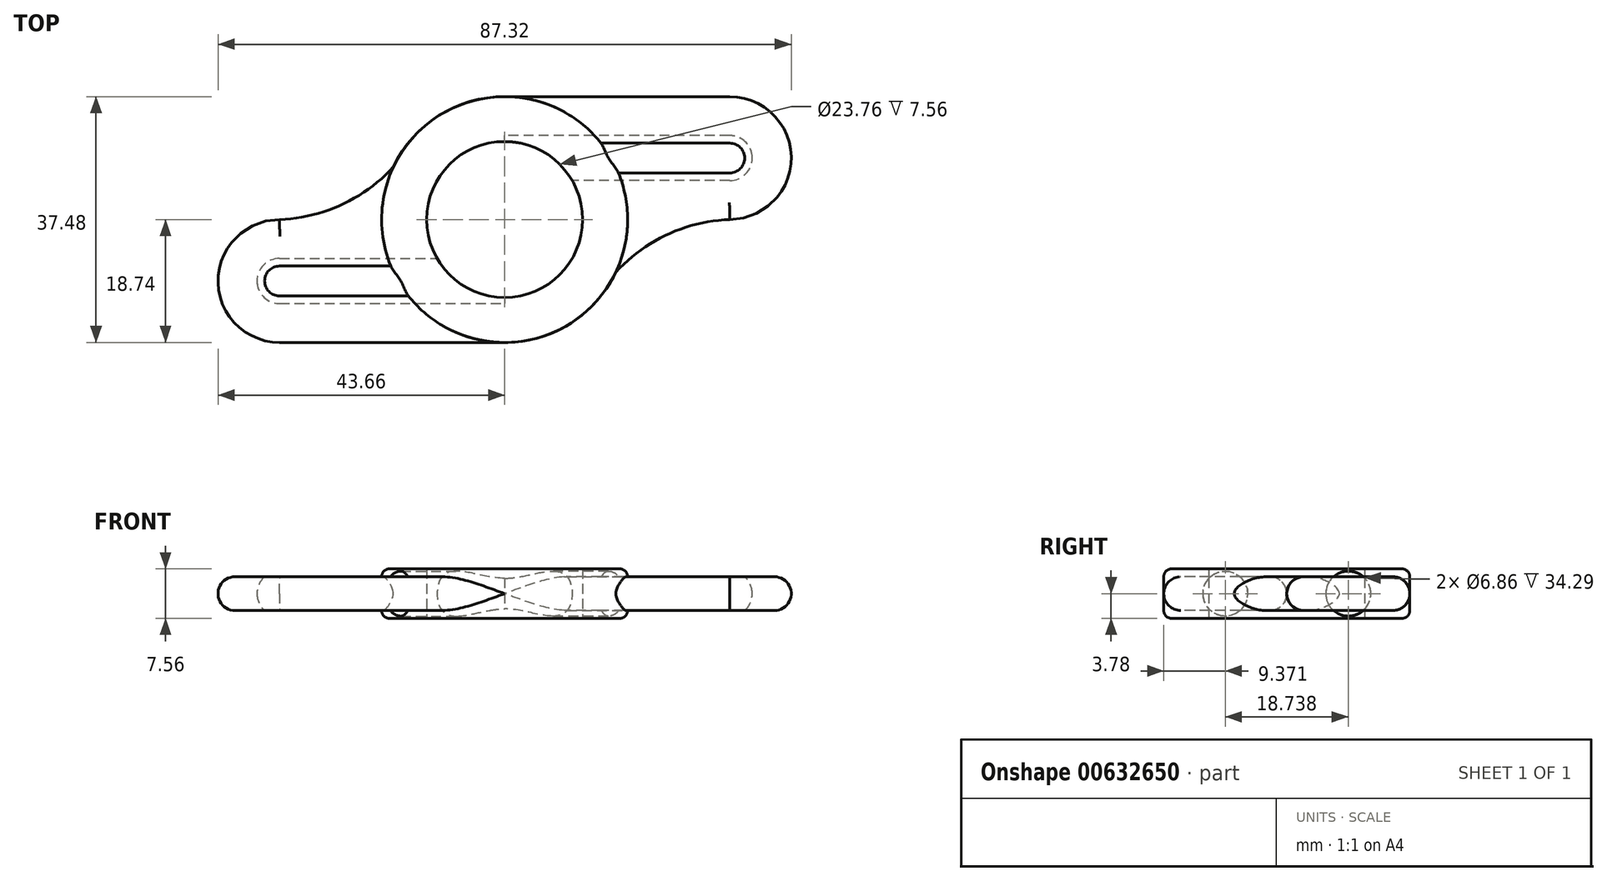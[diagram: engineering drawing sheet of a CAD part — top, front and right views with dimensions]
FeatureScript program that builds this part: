
annotation { "Feature Type Name" : "Feature", "Feature Type Description" : "" }
export const myFeature = defineFeature(function(context is Context, id is Id, definition is map)
    precondition{}
    {
        {
            var Q0;
            Q0=qCreatedBy(makeId("Top.planeOp"),FACE);
            var sketch = newSketch(context, id + "F0", { "sketchPlane" : qUnion([Q0])});
            skCircle(sketch, "E0", {"center": v(0, 0) * mm, "radius": 11.88 * mm});
            skCircle(sketch, "E1", {"center": v(0, 0) * mm, "radius": 18.74 * mm});
            skLineSegment(sketch, "E2", {"start": v(0, 0) * mm, "end": v(0, -18.74) * mm});
            skLineSegment(sketch, "E3", {"start": v(0, -18.74) * mm, "end": v(-34.3, -18.74) * mm});
            skLineSegment(sketch, "E4", {"start": v(-34.3, -18.74) * mm, "end": v(-34.3, 0) * mm});
            skLineSegment(sketch, "E5", {"start": v(-34.3, 0) * mm, "end": v(0, 0) * mm});
            skPoint(sketch, "E6", {"position": v(-34.3, -9.37) * mm});
            skCircle(sketch, "E7", {"center": v(-34.3, -9.37) * mm, "radius": 9.37 * mm});
            skLineSegment(sketch, "E8", {"start": v(0, 0) * mm, "end": v(0, 18.74) * mm});
            skLineSegment(sketch, "E9", {"start": v(0, 18.74) * mm, "end": v(34.3, 18.74) * mm});
            skLineSegment(sketch, "E10", {"start": v(34.3, 18.74) * mm, "end": v(34.3, 0) * mm});
            skLineSegment(sketch, "E11", {"start": v(34.3, 0) * mm, "end": v(0, 0) * mm});
            skPoint(sketch, "E12", {"position": v(34.3, 9.37) * mm});
            skCircle(sketch, "E13", {"center": v(34.3, 9.37) * mm, "radius": 9.37 * mm});
            skLineSegment(sketch, "E14", {"start": v(-18.74, 0) * mm, "end": v(-18.74, 17.97) * mm});
            skLineSegment(sketch, "E15", {"start": v(18.74, 0) * mm, "end": v(18.74, -17.25) * mm});
            skPoint(sketch, "E16", {"position": v(-18.74, 6.25) * mm});
            skPoint(sketch, "E17", {"position": v(18.74, -6.25) * mm});
            skLineSegment(sketch, "E18", {"start": v(0, 0) * mm, "end": v(-13.25, 13.25) * mm});
            skLineSegment(sketch, "E19", {"start": v(0, 0) * mm, "end": v(13.25, -13.25) * mm});
            skArc(sketch, "E20", {"start": v(-34.3, 0) * mm, "mid": v(-24.81, 2.27) * mm, "end": v(-16.94, 8.02) * mm});
            skArc(sketch, "E21", {"start": v(34.3, 0) * mm, "mid": v(24.81, -2.27) * mm, "end": v(16.94, -8.02) * mm});
            skSolve(sketch);
        }
        {
            var Q0;
            {var subQ3=sQuery(id+"F0.wireOp",EDGE,"E0");var subQ5=sQuery(id+"F0.wireOp",EDGE,"E18");var subQ8=makeQuery(id+"F0.imprint","INTERSECT",VERTEX,{"derivedFrom":[subQ3,subQ5]});Q0=makeQuery(id+"F0.imprint","IMPRINT",FACE,{"disambiguationData":[TD([[makeQuery(id+"F0.imprint","IMPRINT",EDGE,{"disambiguationData":[TD([[subQ8,-1.0]])],"derivedFrom":subQ3}),-1.0]])]});}
            var Q1;
            {var subQ0=sQuery(id+"F0.wireOp",EDGE,"E8");var subQ1=sQuery(id+"F0.wireOp",EDGE,"E0");var subQ2=makeQuery(id+"F0.imprint","INTERSECT",VERTEX,{"derivedFrom":[subQ1,subQ0]});Q1=makeQuery(id+"F0.imprint","IMPRINT",FACE,{"disambiguationData":[TD([[makeQuery(id+"F0.imprint","IMPRINT",EDGE,{"disambiguationData":[TD([[subQ2,-1.0]])],"derivedFrom":subQ1}),-1.0]])]});}
            var Q2;
            {var subQ0=sQuery(id+"F0.wireOp",EDGE,"E8");var subQ1=sQuery(id+"F0.wireOp",EDGE,"E0");var subQ2=makeQuery(id+"F0.imprint","INTERSECT",VERTEX,{"derivedFrom":[subQ1,subQ0]});Q2=makeQuery(id+"F0.imprint","IMPRINT",FACE,{"disambiguationData":[TD([[makeQuery(id+"F0.imprint","IMPRINT",EDGE,{"disambiguationData":[TD([[subQ2,1.0]])],"derivedFrom":subQ1}),-1.0]])]});}
            var Q3;
            {var subQ0=sQuery(id+"F0.wireOp",EDGE,"E11");var subQ3=sQuery(id+"F0.wireOp",EDGE,"E0");var subQ4=makeQuery(id+"F0.imprint","INTERSECT",VERTEX,{"derivedFrom":[subQ3,subQ0]});Q3=makeQuery(id+"F0.imprint","IMPRINT",FACE,{"disambiguationData":[TD([[makeQuery(id+"F0.imprint","IMPRINT",EDGE,{"disambiguationData":[TD([[subQ4,1.0]])],"derivedFrom":subQ3}),-1.0]])]});}
            var Q4;
            {var subQ0=sQuery(id+"F0.wireOp",EDGE,"E2");var subQ1=sQuery(id+"F0.wireOp",EDGE,"E0");var subQ2=makeQuery(id+"F0.imprint","INTERSECT",VERTEX,{"derivedFrom":[subQ1,subQ0]});Q4=makeQuery(id+"F0.imprint","IMPRINT",FACE,{"disambiguationData":[TD([[makeQuery(id+"F0.imprint","IMPRINT",EDGE,{"disambiguationData":[TD([[subQ2,-1.0]])],"derivedFrom":subQ1}),-1.0]])]});}
            var Q5;
            {var subQ0=sQuery(id+"F0.wireOp",EDGE,"E5");var subQ1=sQuery(id+"F0.wireOp",EDGE,"E0");var subQ2=makeQuery(id+"F0.imprint","INTERSECT",VERTEX,{"derivedFrom":[subQ1,subQ0]});Q5=makeQuery(id+"F0.imprint","IMPRINT",FACE,{"disambiguationData":[TD([[makeQuery(id+"F0.imprint","IMPRINT",EDGE,{"disambiguationData":[TD([[subQ2,-1.0]])],"derivedFrom":subQ1}),-1.0]])]});}
            extrude(context, id + "F1", {"entities" : qUnion([Q0, Q1, Q2, Q3, Q4, Q5]), "endBound" : BoundingType.SYMMETRIC, "depth" : 7 * mm * 1.08, "offsetDistance" : 25.4 * mm});
        }
        {
            var Q0;
            {var subQ0=sQuery(id+"F0.wireOp",EDGE,"E9");Q0=makeQuery(id+"F0.imprint","IMPRINT",FACE,{"disambiguationData":[TD([[makeQuery(id+"F0.imprint","IMPRINT",EDGE,{"derivedFrom":subQ0}),-1.0]])]});}
            var Q1;
            {var subQ0=sQuery(id+"F0.wireOp",EDGE,"E10");Q1=makeQuery(id+"F0.imprint","IMPRINT",FACE,{"disambiguationData":[TD([[makeQuery(id+"F0.imprint","IMPRINT",EDGE,{"derivedFrom":subQ0}),-1.0]])]});}
            var Q2;
            {var subQ0=sQuery(id+"F0.wireOp",EDGE,"E10");Q2=makeQuery(id+"F0.imprint","IMPRINT",FACE,{"disambiguationData":[TD([[makeQuery(id+"F0.imprint","IMPRINT",EDGE,{"derivedFrom":subQ0}),1.0]])]});}
            var Q3;
            {var subQ0=sQuery(id+"F0.wireOp",EDGE,"E21");var subQ3=sQuery(id+"F0.wireOp",EDGE,"E15");var subQ5=makeQuery(id+"F0.imprint","INTERSECT",VERTEX,{"derivedFrom":[subQ3,subQ0]});Q3=makeQuery(id+"F0.imprint","IMPRINT",FACE,{"disambiguationData":[TD([[makeQuery(id+"F0.imprint","IMPRINT",EDGE,{"disambiguationData":[TD([[subQ5,1.0]])],"derivedFrom":subQ3}),1.0]])]});}
            var Q4;
            {var subQ1=sQuery(id+"F0.wireOp",EDGE,"E1");var subQ3=sQuery(id+"F0.wireOp",EDGE,"E21");var subQ4=makeQuery(id+"F0.imprint","INTERSECT",VERTEX,{"derivedFrom":[subQ1,subQ3]});Q4=makeQuery(id+"F0.imprint","IMPRINT",FACE,{"disambiguationData":[TD([[makeQuery(id+"F0.imprint","IMPRINT",EDGE,{"disambiguationData":[TD([[subQ4,1.0]])],"derivedFrom":subQ3}),-1.0]])]});}
            var Q5;
            {var subQ0=sQuery(id+"F0.wireOp",EDGE,"E3");Q5=makeQuery(id+"F0.imprint","IMPRINT",FACE,{"disambiguationData":[TD([[makeQuery(id+"F0.imprint","IMPRINT",EDGE,{"derivedFrom":subQ0}),-1.0]])]});}
            var Q6;
            {var subQ0=sQuery(id+"F0.wireOp",EDGE,"E20");var subQ3=sQuery(id+"F0.wireOp",EDGE,"E14");var subQ5=makeQuery(id+"F0.imprint","INTERSECT",VERTEX,{"derivedFrom":[subQ3,subQ0]});Q6=makeQuery(id+"F0.imprint","IMPRINT",FACE,{"disambiguationData":[TD([[makeQuery(id+"F0.imprint","IMPRINT",EDGE,{"disambiguationData":[TD([[subQ5,1.0]])],"derivedFrom":subQ3}),1.0]])]});}
            var Q7;
            {var subQ1=sQuery(id+"F0.wireOp",EDGE,"E1");var subQ3=sQuery(id+"F0.wireOp",EDGE,"E20");var subQ4=makeQuery(id+"F0.imprint","INTERSECT",VERTEX,{"derivedFrom":[subQ1,subQ3]});Q7=makeQuery(id+"F0.imprint","IMPRINT",FACE,{"disambiguationData":[TD([[makeQuery(id+"F0.imprint","IMPRINT",EDGE,{"disambiguationData":[TD([[subQ4,1.0]])],"derivedFrom":subQ3}),-1.0]])]});}
            var Q8;
            {var subQ0=sQuery(id+"F0.wireOp",EDGE,"E4");Q8=makeQuery(id+"F0.imprint","IMPRINT",FACE,{"disambiguationData":[TD([[makeQuery(id+"F0.imprint","IMPRINT",EDGE,{"derivedFrom":subQ0}),-1.0]])]});}
            var Q9;
            {var subQ0=sQuery(id+"F0.wireOp",EDGE,"E4");Q9=makeQuery(id+"F0.imprint","IMPRINT",FACE,{"disambiguationData":[TD([[makeQuery(id+"F0.imprint","IMPRINT",EDGE,{"derivedFrom":subQ0}),1.0]])]});}
            extrude(context, id + "F2", {"entities" : qUnion([Q0, Q1, Q2, Q3, Q4, Q5, Q6, Q7, Q8, Q9]), "operationType" : NewBodyOperationType.ADD, "endBound" : BoundingType.SYMMETRIC, "depth" : (6.35 * mm * (3 / 4)) * 1.08, "offsetDistance" : 25.4 * mm});
        }
        {
            var Q0;
            Q0=qCreatedBy(makeId("Top.planeOp"),FACE);
            var sketch = newSketch(context, id + "F3", { "sketchPlane" : qUnion([Q0])});
            skPoint(sketch, "E22", {"position": v(34.3, 9.37) * mm});
            skCircle(sketch, "E23", {"center": v(34.3, 9.37) * mm, "radius": 3.43 * mm});
            skLineSegment(sketch, "E24", {"start": v(34.3, 9.37) * mm, "end": v(34.3, 12.8) * mm});
            skLineSegment(sketch, "E25", {"start": v(34.3, 12.8) * mm, "end": v(0, 12.8) * mm});
            skLineSegment(sketch, "E26", {"start": v(34.3, 9.37) * mm, "end": v(0, 9.37) * mm});
            skLineSegment(sketch, "E27", {"start": v(0, 9.37) * mm, "end": v(0, 12.8) * mm});
            skLineSegment(sketch, "E28", {"start": v(34.3, 9.37) * mm, "end": v(37.72, 9.37) * mm});
            skSolve(sketch);
        }
        {
            var Q0;
            {var subQ0=sQuery(id+"F3.wireOp",EDGE,"E25");Q0=makeQuery(id+"F3.imprint","IMPRINT",FACE,{"disambiguationData":[TD([[makeQuery(id+"F3.imprint","IMPRINT",EDGE,{"derivedFrom":subQ0}),1.0]])]});}
            var Q1;
            {var subQ0=sQuery(id+"F3.wireOp",EDGE,"E24");Q1=makeQuery(id+"F3.imprint","IMPRINT",FACE,{"disambiguationData":[TD([[makeQuery(id+"F3.imprint","IMPRINT",EDGE,{"derivedFrom":subQ0}),1.0]])]});}
            var Q2;
            {var subQ0=sQuery(id+"F3.wireOp",EDGE,"E24");Q2=makeQuery(id+"F3.imprint","IMPRINT",FACE,{"disambiguationData":[TD([[makeQuery(id+"F3.imprint","IMPRINT",EDGE,{"derivedFrom":subQ0}),-1.0]])]});}
            var Q3;
            Q3=sQuery(id+"F3.wireOp",EDGE,"E26");
            revolve(context, id + "F4", {"operationType" : NewBodyOperationType.REMOVE, "entities" : qUnion([Q0, Q1, Q2]), "axis" : qUnion([Q3]), "revolveType" : RevolveType.FULL, "oppositeDirection" : true});
        }
        {
            var Q0;
            Q0=qCreatedBy(makeId("Top.planeOp"),FACE);
            var sketch = newSketch(context, id + "F5", { "sketchPlane" : qUnion([Q0])});
            skPoint(sketch, "E29", {"position": v(-34.3, -9.37) * mm});
            skCircle(sketch, "E30", {"center": v(-34.3, -9.37) * mm, "radius": 3.43 * mm});
            skLineSegment(sketch, "E31", {"start": v(-34.3, -9.37) * mm, "end": v(-34.3, -12.8) * mm});
            skLineSegment(sketch, "E32", {"start": v(-34.3, -12.8) * mm, "end": v(0, -12.8) * mm});
            skLineSegment(sketch, "E33", {"start": v(-34.3, -9.37) * mm, "end": v(0, -9.37) * mm});
            skLineSegment(sketch, "E34", {"start": v(0, -9.37) * mm, "end": v(0, -12.8) * mm});
            skLineSegment(sketch, "E35", {"start": v(-34.3, -9.37) * mm, "end": v(-37.72, -9.37) * mm});
            skSolve(sketch);
        }
        {
            var Q0;
            {var subQ0=sQuery(id+"F5.wireOp",EDGE,"E32");Q0=makeQuery(id+"F5.imprint","IMPRINT",FACE,{"disambiguationData":[TD([[makeQuery(id+"F5.imprint","IMPRINT",EDGE,{"derivedFrom":subQ0}),1.0]])]});}
            var Q1;
            {var subQ0=sQuery(id+"F5.wireOp",EDGE,"E31");Q1=makeQuery(id+"F5.imprint","IMPRINT",FACE,{"disambiguationData":[TD([[makeQuery(id+"F5.imprint","IMPRINT",EDGE,{"derivedFrom":subQ0}),1.0]])]});}
            var Q2;
            {var subQ0=sQuery(id+"F5.wireOp",EDGE,"E31");Q2=makeQuery(id+"F5.imprint","IMPRINT",FACE,{"disambiguationData":[TD([[makeQuery(id+"F5.imprint","IMPRINT",EDGE,{"derivedFrom":subQ0}),-1.0]])]});}
            var Q3;
            Q3=sQuery(id+"F5.wireOp",EDGE,"E33");
            revolve(context, id + "F6", {"operationType" : NewBodyOperationType.REMOVE, "entities" : qUnion([Q0, Q1, Q2]), "axis" : qUnion([Q3]), "revolveType" : RevolveType.FULL, "oppositeDirection" : true});
        }
        {
            var Q0;
            Q0=makeQuery(id+"F2.opExtrude","CAP_EDGE",EDGE,{"disambiguationData":[OSD([sQuery(id+"F0.wireOp",EDGE,"E9")])],"isStart":false});
            var Q1;
            Q1=makeQuery(id+"F2.opExtrude","CAP_EDGE",EDGE,{"disambiguationData":[OSD([sQuery(id+"F0.wireOp",EDGE,"E20")])],"isStart":false});
            var Q2;
            Q2=makeQuery(id+"F2.opExtrude","CAP_EDGE",EDGE,{"disambiguationData":[OSD([sQuery(id+"F0.wireOp",EDGE,"E3")])],"isStart":false});
            var Q3;
            Q3=makeQuery(id+"F2.opExtrude","CAP_EDGE",EDGE,{"disambiguationData":[OSD([sQuery(id+"F0.wireOp",EDGE,"E3")])],"isStart":true});
            var Q4;
            Q4=makeQuery(id+"F2.opExtrude","CAP_EDGE",EDGE,{"disambiguationData":[OSD([sQuery(id+"F0.wireOp",EDGE,"E9")])],"isStart":true});
            fillet(context, id + "F7", {"entities" : qUnion([Q0, Q1, Q2, Q3, Q4]), "radius" : (6.35 * mm * (3 / 4)) * 1.08 / 2, "tangentPropagation" : true, "allowEdgeOverflow" : false});
        }
        {
            var Q0;
            Q0=makeQuery(id+"F1.opExtrude","CAP_EDGE",EDGE,{"disambiguationData":[OSD([sQuery(id+"F0.wireOp",EDGE,"E1")])],"isStart":false});
            var Q1;
            Q1=makeQuery(id+"F1.opExtrude","CAP_EDGE",EDGE,{"disambiguationData":[OSD([sQuery(id+"F0.wireOp",EDGE,"E1")])],"isStart":true});
            fillet(context, id + "F8", {"entities" : qUnion([Q0, Q1]), "radius" : 1.22 * mm, "tangentPropagation" : true, "allowEdgeOverflow" : false});
        }
    });
